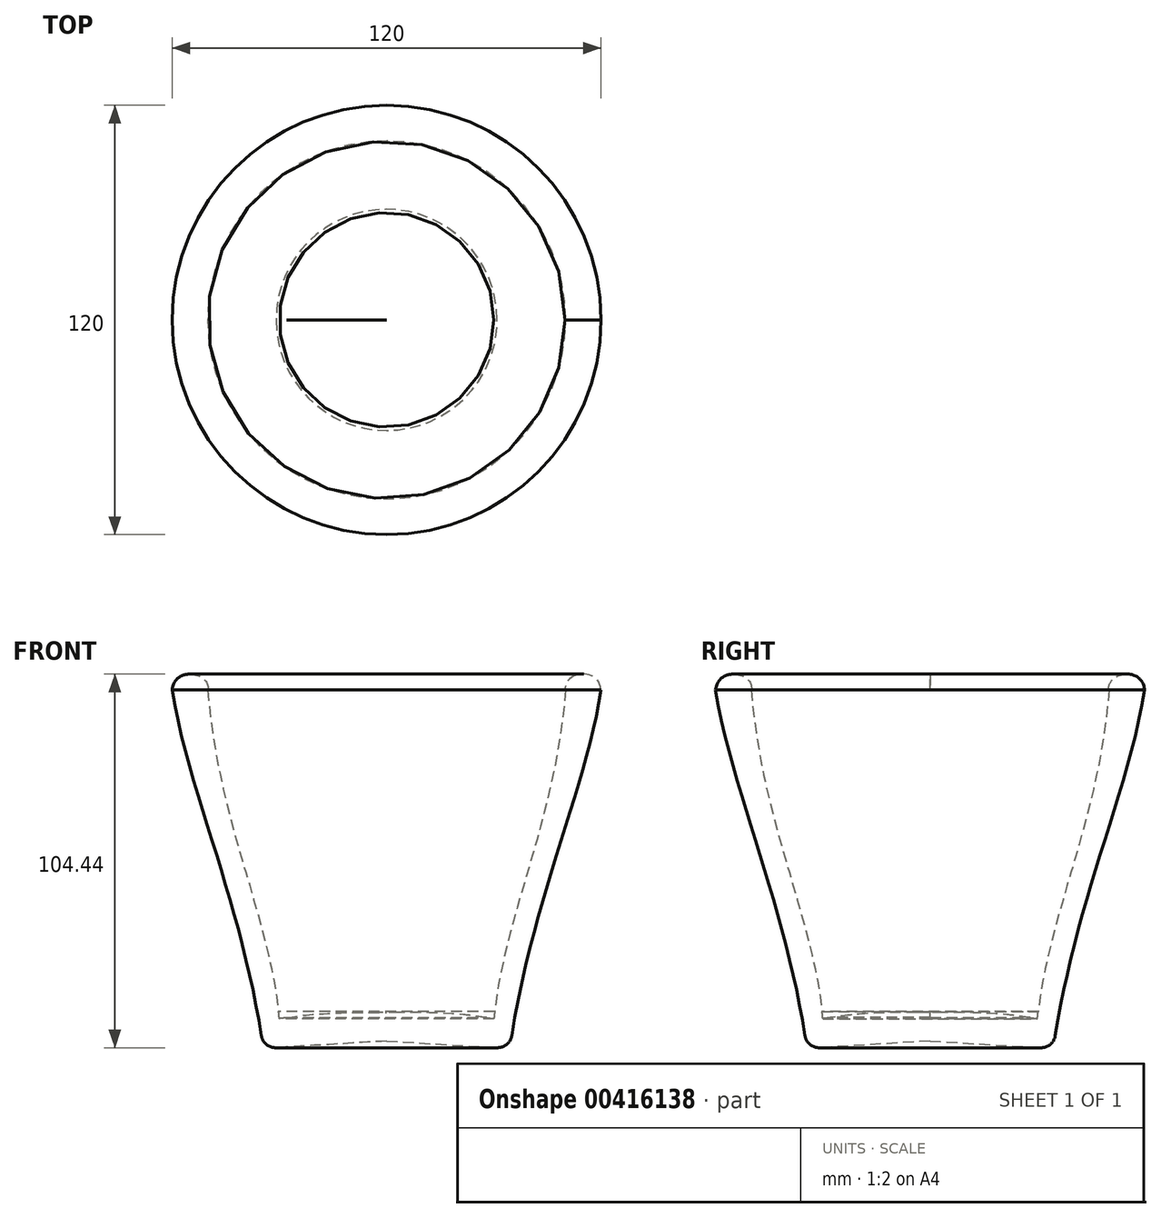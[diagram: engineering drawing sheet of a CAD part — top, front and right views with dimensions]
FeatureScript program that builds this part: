
annotation { "Feature Type Name" : "Feature", "Feature Type Description" : "" }
export const myFeature = defineFeature(function(context is Context, id is Id, definition is map)
    precondition{}
    {
        {
            var Q0;
            Q0=qCreatedBy(makeId("Front.planeOp"),FACE);
            var sketch = newSketch(context, id + "F0", { "sketchPlane" : qUnion([Q0])});
            skLineSegment(sketch, "E0", {"start": v(0, 90.6) * mm, "end": v(0, -94.06) * mm, "construction": true});
            skFitSpline(sketch, "E1", {"points": [v(-60, 47.38) * mm, v(-34.46, -52.78) * mm], "startDerivative": vector(13.98, -86.63) * mm, "endDerivative": vector(17.91, -122.57) * mm});
            skFitSpline(sketch, "E2", {"points": [v(-60, 47.38) * mm, v(-50, 47.38) * mm], "startDerivative": vector(2.4, 20.81) * mm, "endDerivative": vector(-2.51, -14.4) * mm});
            skFitSpline(sketch, "E3", {"points": [v(-50, 47.38) * mm, v(-30, -44.5) * mm], "startDerivative": vector(8.1, -109.66) * mm, "endDerivative": vector(8.55, -87.57) * mm});
            skFitSpline(sketch, "E4", {"points": [v(-30, -44.5) * mm, v(0, -42.76) * mm], "startDerivative": vector(21.98, 2.9) * mm, "endDerivative": vector(57.86, -0.4) * mm});
            skArc(sketch, "E5.filletArc", {"start": v(-35, -49.26) * mm, "mid": v(-33.59, -51.72) * mm, "end": v(-30.9, -52.62) * mm});
            skLineSegment(sketch, "E6", {"start": v(0, -50.76) * mm, "end": v(0, -42.76) * mm});
            skArc(sketch, "E7.filletArc", {"start": v(-30.22, -42.48) * mm, "mid": v(-29.45, -43.83) * mm, "end": v(-27.95, -44.23) * mm});
            skLineSegment(sketch, "E8", {"start": v(-30.9, -52.62) * mm, "end": v(0, -50.76) * mm});
            skSolve(sketch);
        }
        {
            var Q0;
            Q0=makeQuery(id+"F0.imprint","IMPRINT",FACE,{"disambiguationData":[TD([[makeQuery(id+"F0.imprint","IMPRINT",EDGE,{"derivedFrom":sQuery(id+"F0.wireOp",EDGE,"E1")}),1.0]])]});
            var Q1;
            Q1=sQuery(id+"F0.wireOp",EDGE,"E0");
            revolve(context, id + "F1", {"entities" : qUnion([Q0]), "axis" : qUnion([Q1]), "revolveType" : RevolveType.FULL});
        }
        {
            var Q0;
            Q0=qCreatedBy(makeId("Right.planeOp"),FACE);
            var sketch = newSketch(context, id + "F2", { "sketchPlane" : qUnion([Q0])});
            skFitSpline(sketch, "E9", {"points": [v(-48.34, 26.07) * mm, v(-36.8, -35.76) * mm], "startDerivative": vector(-78.59, 54.67) * mm, "endDerivative": vector(164, -56.13) * mm});
            skSolve(sketch);
        }
    });
